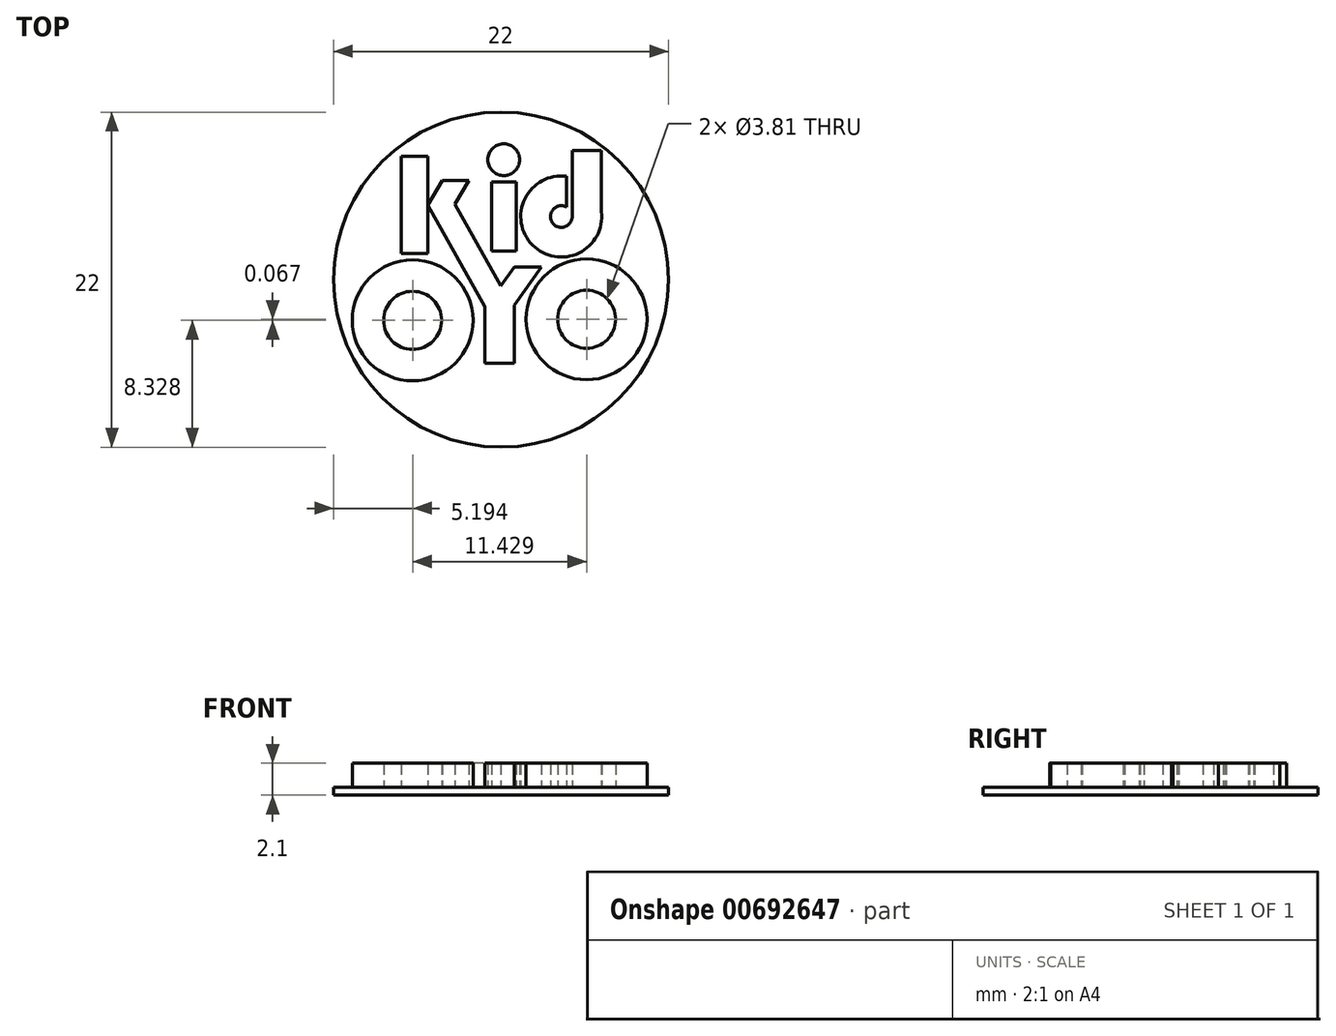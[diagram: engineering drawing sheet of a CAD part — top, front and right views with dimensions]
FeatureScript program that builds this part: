
annotation { "Feature Type Name" : "Feature", "Feature Type Description" : "" }
export const myFeature = defineFeature(function(context is Context, id is Id, definition is map)
    precondition{}
    {
        {
            var Q0;
            Q0=qCreatedBy(makeId("Top.planeOp"),FACE);
            var sketch = newSketch(context, id + "F0", { "sketchPlane" : qUnion([Q0])});
            skCircle(sketch, "E0", {"center": v(0, 0) * mm, "radius": 11 * mm});
            skSolve(sketch);
        }
        {
            var Q0;
            Q0=makeQuery(id+"F0.imprint","IMPRINT",FACE,{"disambiguationData":[TD([[makeQuery(id+"F0.imprint","IMPRINT",EDGE,{"derivedFrom":sQuery(id+"F0.wireOp",EDGE,"E0")}),1.0]])]});
            extrude(context, id + "F1", {"entities" : qUnion([Q0]), "oppositeDirection" : true, "depth" : 0.5 * mm, "offsetDistance" : 25.4 * mm});
        }
        {
            var Q0;
            Q0=qCreatedBy(makeId("Top.planeOp"),FACE);
            var sketch = newSketch(context, id + "F2", { "sketchPlane" : qUnion([Q0])});
            skLineSegment(sketch, "E1.bottom", {"start": v(-0.85, -4.4) * mm, "end": v(0.7, -4.4) * mm});
            skLineSegment(sketch, "E1.left", {"start": v(-0.85, -4.4) * mm, "end": v(-0.85, -1.43) * mm});
            skLineSegment(sketch, "E1.right", {"start": v(0.7, -4.4) * mm, "end": v(0.7, -1.35) * mm});
            skLineSegment(sketch, "E2", {"start": v(0.7, -1.35) * mm, "end": v(2.12, 0.65) * mm});
            skLineSegment(sketch, "E3", {"start": v(2.12, 0.65) * mm, "end": v(0.7, 0.65) * mm});
            skLineSegment(sketch, "E4", {"start": v(0.7, 0.65) * mm, "end": v(0, -0.34) * mm});
            skLineSegment(sketch, "E5", {"start": v(0, -0.34) * mm, "end": v(-2.41, 3.97) * mm});
            skLineSegment(sketch, "E6", {"start": v(-2.41, 3.97) * mm, "end": v(-1.7, 5.2) * mm});
            skLineSegment(sketch, "E7", {"start": v(-1.7, 5.2) * mm, "end": v(-3.1, 5.2) * mm});
            skLineSegment(sketch, "E8.bottom", {"start": v(-5.25, 1.37) * mm, "end": v(-3.85, 1.37) * mm});
            skLineSegment(sketch, "E8.top", {"start": v(-5.25, 6.47) * mm, "end": v(-3.85, 6.47) * mm});
            skLineSegment(sketch, "E8.left", {"start": v(-5.25, 1.37) * mm, "end": v(-5.25, 6.47) * mm});
            skLineSegment(sketch, "E9.bottom", {"start": v(-0.5, 1.5) * mm, "end": v(0.8, 1.5) * mm});
            skLineSegment(sketch, "E9.top", {"start": v(-0.5, 5.13) * mm, "end": v(0.8, 5.13) * mm});
            skLineSegment(sketch, "E9.left", {"start": v(-0.5, 1.5) * mm, "end": v(-0.5, 5.13) * mm});
            skLineSegment(sketch, "E9.right", {"start": v(0.8, 1.5) * mm, "end": v(0.8, 5.13) * mm});
            skCircle(sketch, "E10", {"center": v(0.15, 6.3) * mm, "radius": 0.84 * mm});
            skCircle(sketch, "E11", {"center": v(-4.64, -2.14) * mm, "radius": 3.18 * mm});
            skCircle(sketch, "E12", {"center": v(4.5, -2.08) * mm, "radius": 3.18 * mm});
            skCircle(sketch, "E13", {"center": v(4.5, -2.08) * mm, "radius": 1.52 * mm});
            skCircle(sketch, "E14", {"center": v(-4.64, -2.14) * mm, "radius": 1.52 * mm});
            skArc(sketch, "E15", {"start": v(3.43, 5.43) * mm, "mid": v(1.66, 1.81) * mm, "end": v(5.28, 3.57) * mm});
            skArc(sketch, "E16", {"start": v(3.43, 3.82) * mm, "mid": v(2.68, 3.02) * mm, "end": v(3.74, 3.33) * mm});
            skLineSegment(sketch, "E17.top", {"start": v(3.74, 6.78) * mm, "end": v(5.28, 6.78) * mm});
            skLineSegment(sketch, "E17.right", {"start": v(5.28, 3.57) * mm, "end": v(5.28, 6.78) * mm});
            skLineSegment(sketch, "E18", {"start": v(3.43, 3.82) * mm, "end": v(3.43, 5.43) * mm});
            skLineSegment(sketch, "E19", {"start": v(3.74, 3.33) * mm, "end": v(3.74, 3.3) * mm});
            skLineSegment(sketch, "E20", {"start": v(-3.85, 6.47) * mm, "end": v(-3.85, 1.37) * mm});
            skLineSegment(sketch, "E21", {"start": v(-3.85, 3.92) * mm, "end": v(-3.1, 5.2) * mm});
            skLineSegment(sketch, "E22", {"start": v(-3.85, 3.92) * mm, "end": v(-0.85, -1.43) * mm});
            skLineSegment(sketch, "E23", {"start": v(3.74, 3.33) * mm, "end": v(3.74, 6.78) * mm});
            skSolve(sketch);
        }
        {
            var Q0;
            Q0=qSketchRegion(id+"F2",true);
            extrude(context, id + "F3", {"entities" : qUnion([Q0]), "depth" : 1.27 * mm, "offsetDistance" : 25.4 * mm});
        }
        {
            var Q0;
            Q0=makeQuery(id+"F3.opExtrude","SWEPT_BODY",BODY,{"disambiguationData":[OSD([sQuery(id+"F2.wireOp",EDGE,"E8.bottom"),sQuery(id+"F2.wireOp",EDGE,"E8.top"),sQuery(id+"F2.wireOp",EDGE,"E8.left"),sQuery(id+"F2.wireOp",EDGE,"E20")])]});
            var Q1;
            Q1=makeQuery(id+"F3.opExtrude","SWEPT_BODY",BODY,{"disambiguationData":[OSD([sQuery(id+"F2.wireOp",EDGE,"E1.bottom"),sQuery(id+"F2.wireOp",EDGE,"E1.left"),sQuery(id+"F2.wireOp",EDGE,"E1.right"),sQuery(id+"F2.wireOp",EDGE,"E2"),sQuery(id+"F2.wireOp",EDGE,"E3"),sQuery(id+"F2.wireOp",EDGE,"E4"),sQuery(id+"F2.wireOp",EDGE,"E5"),sQuery(id+"F2.wireOp",EDGE,"E6"),sQuery(id+"F2.wireOp",EDGE,"E7"),sQuery(id+"F2.wireOp",EDGE,"E21"),sQuery(id+"F2.wireOp",EDGE,"E22")])]});
            var Q2;
            Q2=makeQuery(id+"F3.opExtrude","SWEPT_BODY",BODY,{"disambiguationData":[OSD([sQuery(id+"F2.wireOp",EDGE,"E9.bottom"),sQuery(id+"F2.wireOp",EDGE,"E9.top"),sQuery(id+"F2.wireOp",EDGE,"E9.left"),sQuery(id+"F2.wireOp",EDGE,"E9.right")])]});
            var Q3;
            Q3=makeQuery(id+"F3.opExtrude","SWEPT_BODY",BODY,{"disambiguationData":[OSD([sQuery(id+"F2.wireOp",EDGE,"E10")])]});
            var Q4;
            Q4=makeQuery(id+"F3.opExtrude","SWEPT_BODY",BODY,{"disambiguationData":[OSD([sQuery(id+"F2.wireOp",EDGE,"E15"),sQuery(id+"F2.wireOp",EDGE,"E16"),sQuery(id+"F2.wireOp",EDGE,"E17.top"),sQuery(id+"F2.wireOp",EDGE,"E17.left"),sQuery(id+"F2.wireOp",EDGE,"E17.right"),sQuery(id+"F2.wireOp",EDGE,"E18"),sQuery(id+"F2.wireOp",EDGE,"E19")])]});
            var Q5;
            Q5=makeQuery(id+"F3.opExtrude","SWEPT_BODY",BODY,{"disambiguationData":[OSD([sQuery(id+"F2.wireOp",EDGE,"E12"),sQuery(id+"F2.wireOp",EDGE,"E13")])]});
            var Q6;
            Q6=makeQuery(id+"F3.opExtrude","SWEPT_BODY",BODY,{"disambiguationData":[OSD([sQuery(id+"F2.wireOp",EDGE,"E11"),sQuery(id+"F2.wireOp",EDGE,"E14")])]});
            var Q7;
            Q7=qCreatedBy(makeId("Origin.pointOp"),VERTEX);
            transform(context, id + "F4", {"entities" : qUnion([Q0, Q1, Q2, Q3, Q4, Q5, Q6]), "transformType" : TransformType.SCALE_UNIFORMLY, "scale" : 1.25, "scalePoint" : qUnion([Q7]), "makeCopy" : false});
        }
    });
